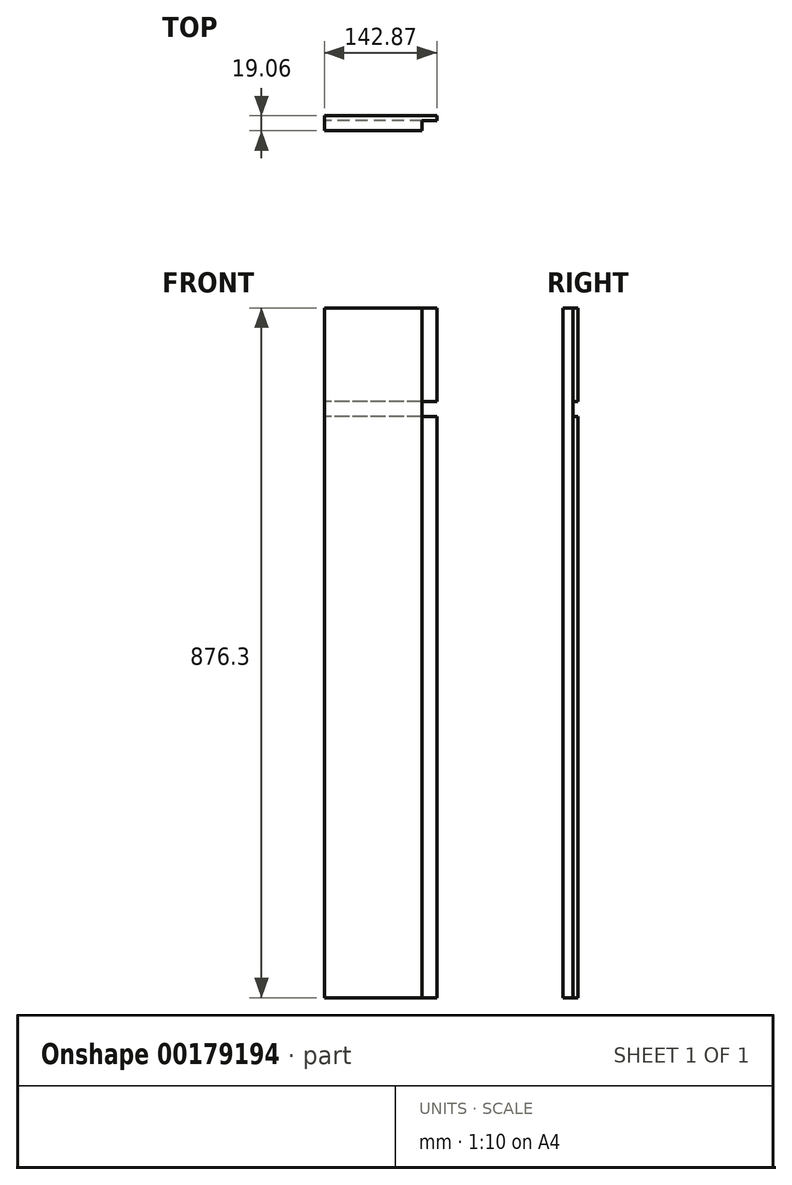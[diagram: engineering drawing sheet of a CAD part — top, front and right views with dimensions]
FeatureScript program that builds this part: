
annotation { "Feature Type Name" : "Feature", "Feature Type Description" : "" }
export const myFeature = defineFeature(function(context is Context, id is Id, definition is map)
    precondition{}
    {
        {
            var Q0;
            Q0=qCreatedBy(makeId("Front.planeOp"),FACE);
            var sketch = newSketch(context, id + "F0", { "sketchPlane" : qUnion([Q0])});
            skLineSegment(sketch, "E0.bottom", {"start": v(-247.9, 438.15) * mm, "end": v(-105.03, 438.15) * mm});
            skLineSegment(sketch, "E0.top", {"start": v(-247.9, -438.15) * mm, "end": v(-105.03, -438.15) * mm});
            skLineSegment(sketch, "E0.left", {"start": v(-247.9, 438.15) * mm, "end": v(-247.9, -438.15) * mm});
            skLineSegment(sketch, "E0.right", {"start": v(-105.03, 438.15) * mm, "end": v(-105.03, -438.15) * mm});
            skLineSegment(sketch, "E1", {"start": v(-247.9, 0) * mm, "end": v(-105.03, 0) * mm});
            skSolve(sketch);
        }
        {
            var Q0;
            {var subQ0=sQuery(id+"F0.wireOp",EDGE,"E0.bottom");Q0=makeQuery(id+"F0.imprint","IMPRINT",FACE,{"disambiguationData":[TD([[makeQuery(id+"F0.imprint","IMPRINT",EDGE,{"derivedFrom":subQ0}),-1.0]])]});}
            var Q1;
            {var subQ0=sQuery(id+"F0.wireOp",EDGE,"E0.top");Q1=makeQuery(id+"F0.imprint","IMPRINT",FACE,{"disambiguationData":[TD([[makeQuery(id+"F0.imprint","IMPRINT",EDGE,{"derivedFrom":subQ0}),1.0]])]});}
            extrude(context, id + "F1", {"entities" : qUnion([Q0, Q1]), "depth" : 19.05 * mm, "symmetric" : true});
        }
        {
            var Q0;
            Q0=makeQuery(id+"F1.opExtrude","CAP_FACE",FACE,{"disambiguationData":[OSD([sQuery(id+"F0.wireOp",EDGE,"E0.bottom"),sQuery(id+"F0.wireOp",EDGE,"E0.top"),sQuery(id+"F0.wireOp",EDGE,"E0.left"),sQuery(id+"F0.wireOp",EDGE,"E0.right")])],"isStart":true});
            var sketch = newSketch(context, id + "F2", { "sketchPlane" : qUnion([Q0])});
            skLineSegment(sketch, "E2.bottom", {"start": v(105.03, 300.04) * mm, "end": v(247.9, 300.04) * mm});
            skLineSegment(sketch, "E2.top", {"start": v(105.03, 319.09) * mm, "end": v(247.9, 319.09) * mm});
            skLineSegment(sketch, "E2.left", {"start": v(105.03, 300.04) * mm, "end": v(105.03, 319.09) * mm});
            skLineSegment(sketch, "E2.right", {"start": v(247.9, 300.04) * mm, "end": v(247.9, 319.09) * mm});
            skSolve(sketch);
        }
        {
            var Q0;
            Q0=makeQuery(id+"F2.imprint","IMPRINT",FACE,{"disambiguationData":[TD([[makeQuery(id+"F2.imprint","IMPRINT",EDGE,{"derivedFrom":sQuery(id+"F2.wireOp",EDGE,"E2.bottom")}),1.0]])]});
            extrude(context, id + "F3", {"entities" : qUnion([Q0]), "operationType" : NewBodyOperationType.REMOVE, "oppositeDirection" : true, "depth" : 6.35 * mm});
        }
        {
            var Q0;
            Q0=makeQuery(id+"F1.opExtrude","CAP_FACE",FACE,{"disambiguationData":[OSD([sQuery(id+"F0.wireOp",EDGE,"E0.bottom"),sQuery(id+"F0.wireOp",EDGE,"E0.top"),sQuery(id+"F0.wireOp",EDGE,"E0.left"),sQuery(id+"F0.wireOp",EDGE,"E0.right")])],"isStart":false});
            var sketch = newSketch(context, id + "F4", { "sketchPlane" : qUnion([Q0])});
            skLineSegment(sketch, "E3.bottom", {"start": v(-105.03, 438.15) * mm, "end": v(-124.08, 438.15) * mm});
            skLineSegment(sketch, "E3.top", {"start": v(-105.03, -438.15) * mm, "end": v(-124.08, -438.15) * mm});
            skLineSegment(sketch, "E3.left", {"start": v(-105.03, 438.15) * mm, "end": v(-105.03, -438.15) * mm});
            skLineSegment(sketch, "E3.right", {"start": v(-124.08, 438.15) * mm, "end": v(-124.08, -438.15) * mm});
            skSolve(sketch);
        }
        {
            var Q0;
            Q0=makeQuery(id+"F4.imprint","IMPRINT",FACE,{"disambiguationData":[TD([[makeQuery(id+"F4.imprint","IMPRINT",EDGE,{"derivedFrom":sQuery(id+"F4.wireOp",EDGE,"Z58Dt405-HxdT-vo11-Jb49-NVRQndEFdQdq.bottom")}),-1.0]])]});
            var Q1;
            Q1=makeQuery(id+"F4.imprint","IMPRINT",FACE,{"disambiguationData":[TD([[makeQuery(id+"F4.imprint","IMPRINT",EDGE,{"derivedFrom":sQuery(id+"F4.wireOp",EDGE,"E3.bottom")}),-1.0]])]});
            extrude(context, id + "F5", {"entities" : qUnion([Q0, Q1]), "operationType" : NewBodyOperationType.REMOVE, "oppositeDirection" : true, "depth" : 12.7 * mm});
        }
    });
